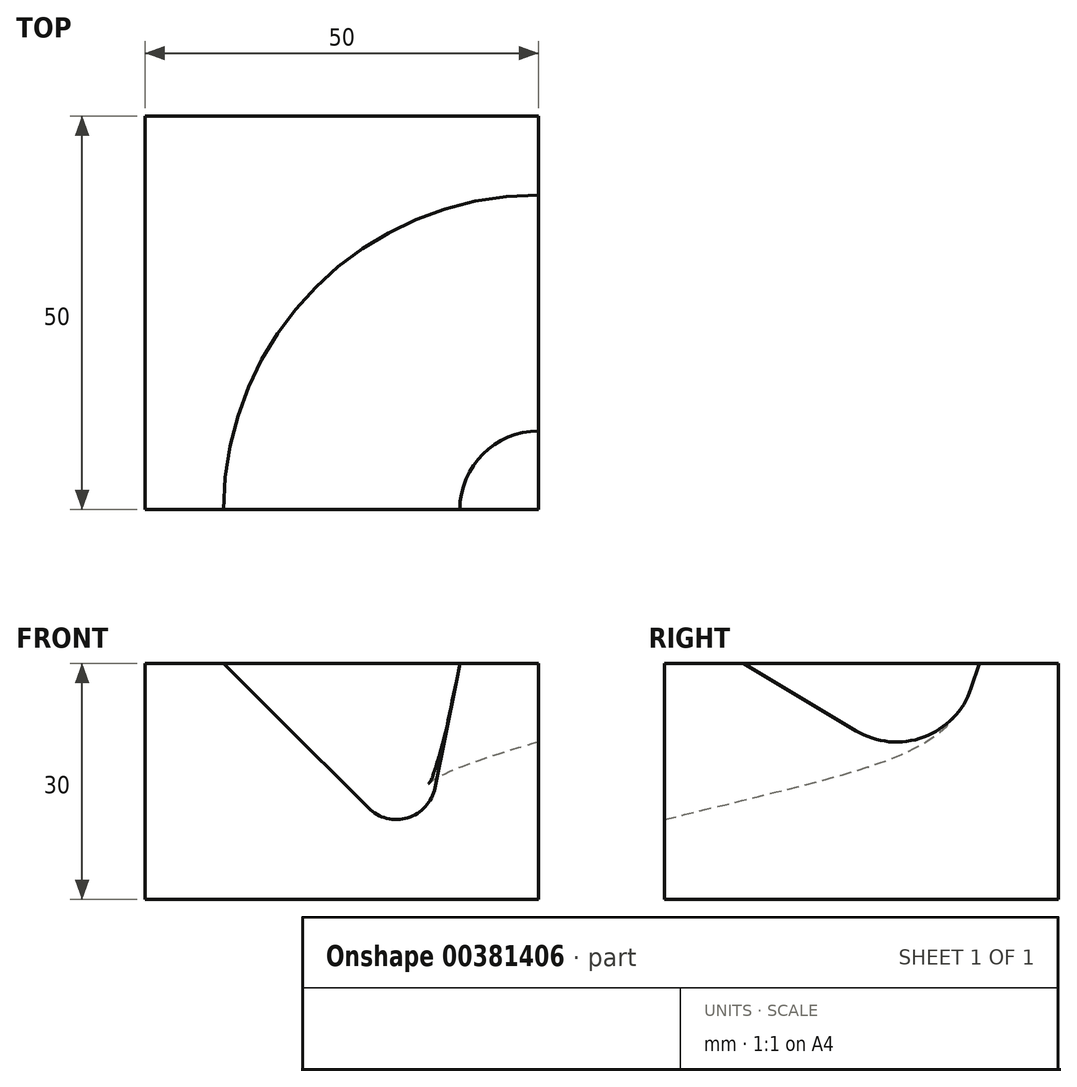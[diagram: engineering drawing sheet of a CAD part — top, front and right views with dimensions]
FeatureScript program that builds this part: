
annotation { "Feature Type Name" : "Feature", "Feature Type Description" : "" }
export const myFeature = defineFeature(function(context is Context, id is Id, definition is map)
    precondition{}
    {
        {
            var Q0;
            Q0=qCreatedBy(makeId("Top.planeOp"),FACE);
            var sketch = newSketch(context, id + "F0", { "sketchPlane" : qUnion([Q0])});
            skLineSegment(sketch, "E0.bottom", {"start": v(-25, 25) * mm, "end": v(25, 25) * mm});
            skLineSegment(sketch, "E0.top", {"start": v(-25, -25) * mm, "end": v(25, -25) * mm});
            skLineSegment(sketch, "E0.left", {"start": v(-25, 25) * mm, "end": v(-25, -25) * mm});
            skLineSegment(sketch, "E0.right", {"start": v(25, 25) * mm, "end": v(25, -25) * mm});
            skPoint(sketch, "E0.middle", {"position": v(0, 0) * mm});
            skSolve(sketch);
        }
        {
            var Q0;
            Q0=makeQuery(id+"F0.imprint","IMPRINT",FACE,{"disambiguationData":[TD([[makeQuery(id+"F0.imprint","IMPRINT",EDGE,{"derivedFrom":sQuery(id+"F0.wireOp",EDGE,"E0.bottom")}),-1.0]])]});
            extrude(context, id + "F1", {"entities" : qUnion([Q0]), "depth" : 30 * mm});
        }
        {
            var Q0;
            Q0=makeQuery(id+"F1.opExtrude","CAP_FACE",FACE,{"disambiguationData":[OSD([sQuery(id+"F0.wireOp",EDGE,"E0.bottom"),sQuery(id+"F0.wireOp",EDGE,"E0.top"),sQuery(id+"F0.wireOp",EDGE,"E0.left"),sQuery(id+"F0.wireOp",EDGE,"E0.right")])],"isStart":false});
            var sketch = newSketch(context, id + "F2", { "sketchPlane" : qUnion([Q0])});
            skArc(sketch, "E1", {"start": v(25, 15) * mm, "mid": v(-3.28, 3.28) * mm, "end": v(-15, -25) * mm});
            skArc(sketch, "E2", {"start": v(25, -15) * mm, "mid": v(17.93, -17.93) * mm, "end": v(15, -25) * mm});
            skSolve(sketch);
        }
        {
            var Q0;
            Q0=makeQuery(id+"F1.opExtrude","SWEPT_FACE",FACE,{"disambiguationData":[OSD([sQuery(id+"F0.wireOp",EDGE,"E0.top")])]});
            var sketch = newSketch(context, id + "F3", { "sketchPlane" : qUnion([Q0])});
            skLineSegment(sketch, "E3", {"start": v(-15, 30) * mm, "end": v(3.4, 11.6) * mm});
            skLineSegment(sketch, "E4", {"start": v(11.83, 14.16) * mm, "end": v(15, 30) * mm});
            skPoint(sketch, "E5.visualSharp", {"position": v(10, 5) * mm});
            skArc(sketch, "E5.filletArc", {"start": v(3.4, 11.6) * mm, "mid": v(8.38, 10.36) * mm, "end": v(11.83, 14.16) * mm});
            skSolve(sketch);
        }
        {
            var Q0;
            Q0=makeQuery(id+"F1.opExtrude","SWEPT_FACE",FACE,{"disambiguationData":[OSD([sQuery(id+"F0.wireOp",EDGE,"E0.right")])]});
            var sketch = newSketch(context, id + "F4", { "sketchPlane" : qUnion([Q0])});
            skLineSegment(sketch, "E6", {"start": v(-15, 30) * mm, "end": v(-0.69, 21.41) * mm});
            skLineSegment(sketch, "E7", {"start": v(13.94, 26.83) * mm, "end": v(15, 30) * mm});
            skPoint(sketch, "E8.visualSharp", {"position": v(10, 15) * mm});
            skArc(sketch, "E8.filletArc", {"start": v(-0.69, 21.41) * mm, "mid": v(7.92, 20.6) * mm, "end": v(13.94, 26.83) * mm});
            skSolve(sketch);
        }
        {
            var Q1;
            {var subQ0=sQuery(id+"F3.wireOp",EDGE,"E3");Q1=makeQuery(id+"F3.imprint","IMPRINT",FACE,{"disambiguationData":[TD([[makeQuery(id+"F3.imprint","IMPRINT",EDGE,{"derivedFrom":subQ0}),1.0]])]});}
            var Q2;
            {var subQ0=sQuery(id+"F4.wireOp",EDGE,"E6");Q2=makeQuery(id+"F4.imprint","IMPRINT",FACE,{"disambiguationData":[TD([[makeQuery(id+"F4.imprint","IMPRINT",EDGE,{"derivedFrom":subQ0}),1.0]])]});}
            var Q3;
            Q3=sQuery(id+"F2.wireOp",EDGE,"E1");
            var Q4;
            Q4=sQuery(id+"F2.wireOp",EDGE,"E2");
            loft(context, id + "F5", {"addGuides" : true, "sheetProfilesArray" : [{ "sheetProfileEntities" : qUnion([Q1]) }, { "sheetProfileEntities" : qUnion([Q2]) }], "guidesArray" : [{ "guideEntities" : qUnion([Q3]), "guideDerivativeType" : LoftGuideDerivativeType.DEFAULT, "guideDerivativeMagnitude" : 1 }, { "guideEntities" : qUnion([Q4]), "guideDerivativeType" : LoftGuideDerivativeType.DEFAULT, "guideDerivativeMagnitude" : 1 }]});
        }
        {
            var Q0;
            {var subQ0=sQuery(id+"F4.wireOp",EDGE,"E6");var subQ3=sQuery(id+"F3.wireOp",EDGE,"E3");Q0=makeQuery(id+"F5.opLoft","SWEPT_BODY",BODY,{"disambiguationData":[OSD([sQuery(id+"F2.wireOp",EDGE,"E1"),sQuery(id+"F2.wireOp",EDGE,"E2"),makeQuery(id+"F3.imprint","IMPRINT",FACE,{"disambiguationData":[TD([[makeQuery(id+"F3.imprint","IMPRINT",EDGE,{"derivedFrom":subQ3}),1.0]])]}),makeQuery(id+"F4.imprint","IMPRINT",FACE,{"disambiguationData":[TD([[makeQuery(id+"F4.imprint","IMPRINT",EDGE,{"derivedFrom":subQ0}),1.0]])]})])]});}
            var Q1;
            Q1=makeQuery(id+"F1.opExtrude","SWEPT_BODY",BODY,{"disambiguationData":[OSD([sQuery(id+"F0.wireOp",EDGE,"E0.bottom"),sQuery(id+"F0.wireOp",EDGE,"E0.top"),sQuery(id+"F0.wireOp",EDGE,"E0.left"),sQuery(id+"F0.wireOp",EDGE,"E0.right")])]});
            booleanBodies(context, id + "F6", {"operationType" : BooleanOperationType.SUBTRACTION, "tools" : qUnion([Q0]), "targets" : qUnion([Q1])});
        }
    });
